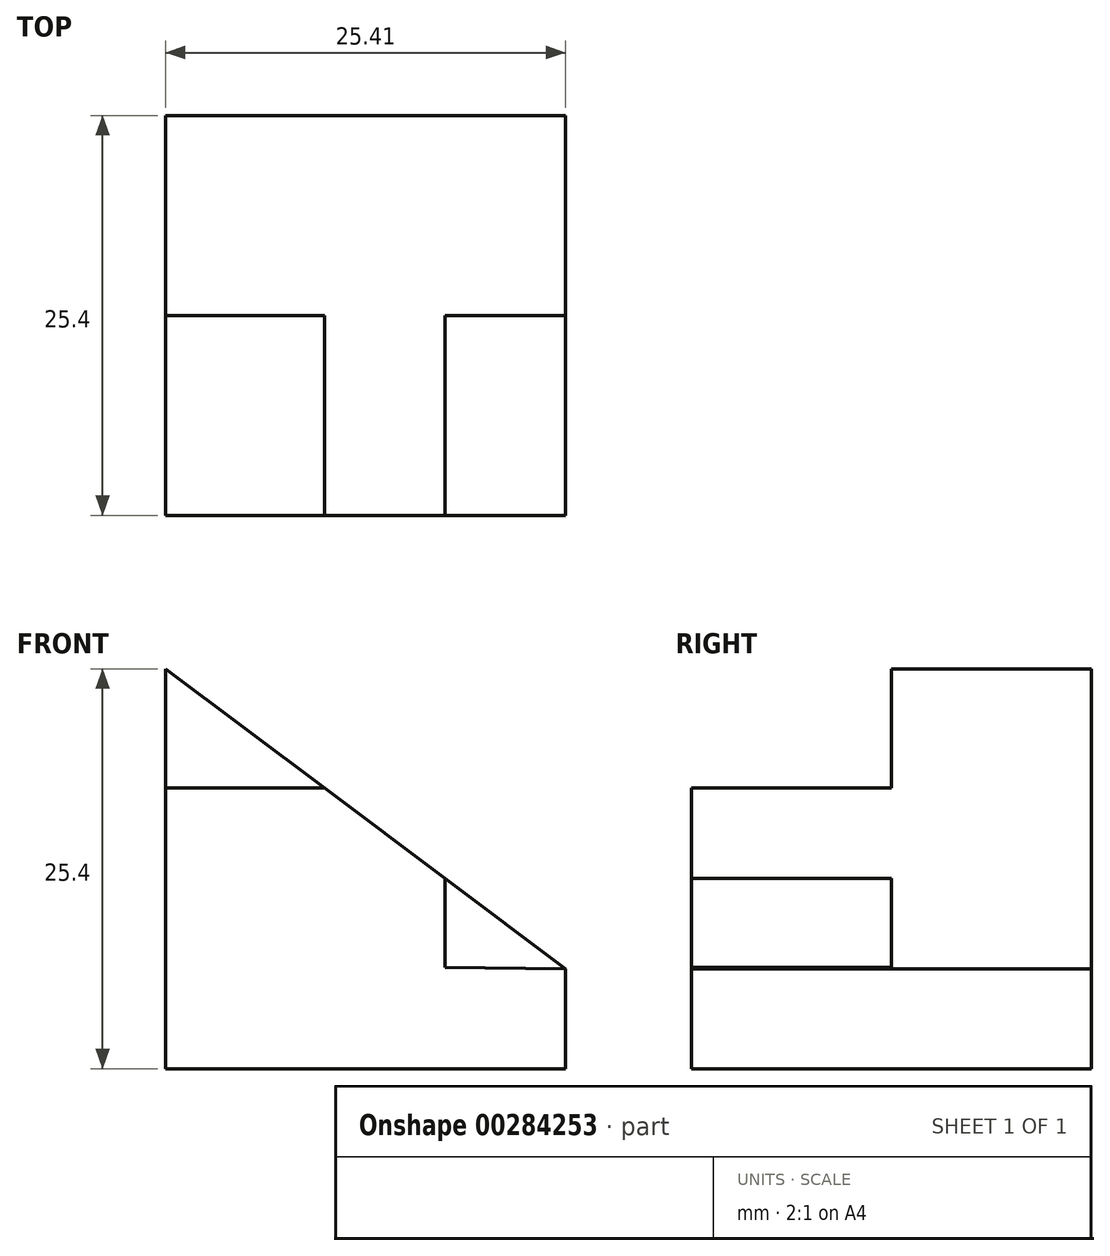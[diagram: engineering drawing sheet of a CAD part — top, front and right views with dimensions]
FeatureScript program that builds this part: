
annotation { "Feature Type Name" : "Feature", "Feature Type Description" : "" }
export const myFeature = defineFeature(function(context is Context, id is Id, definition is map)
    precondition{}
    {
        {
            var Q0;
            Q0=qCreatedBy(makeId("Front.planeOp"),FACE);
            var sketch = newSketch(context, id + "F0", { "sketchPlane" : qUnion([Q0])});
            skLineSegment(sketch, "E0", {"start": v(0, 0) * mm, "end": v(25.4, 0) * mm});
            skLineSegment(sketch, "E1", {"start": v(25.4, 0) * mm, "end": v(25.4, 6.35) * mm});
            skLineSegment(sketch, "E2", {"start": v(25.4, 6.35) * mm, "end": v(0, 6.35) * mm});
            skLineSegment(sketch, "E3", {"start": v(0, 6.35) * mm, "end": v(0, 0) * mm});
            skSolve(sketch);
        }
        {
            var Q0;
            Q0 = qSketchRegion(id + "F0", true);
            extrude(context, id + "F1", {"entities" : qUnion([Q0]), "depth" : 25.4 * mm});
        }
        {
            var Q0;
            Q0=qCreatedBy(makeId("Front.planeOp"),FACE);
            var sketch = newSketch(context, id + "F2", { "sketchPlane" : qUnion([Q0])});
            skLineSegment(sketch, "E4", {"start": v(0, 6.35) * mm, "end": v(0, 25.4) * mm});
            skLineSegment(sketch, "E5", {"start": v(0, 25.4) * mm, "end": v(25.41, 6.35) * mm});
            skLineSegment(sketch, "E6", {"start": v(25.41, 6.35) * mm, "end": v(0, 6.35) * mm});
            skSolve(sketch);
        }
        {
            var Q0;
            Q0=makeQuery(id+"F2.imprint","IMPRINT",FACE,{"disambiguationData":[TD([[makeQuery(id+"F2.imprint","IMPRINT",EDGE,{"derivedFrom":sQuery(id+"F2.wireOp",EDGE,"E4")}),-1.0]])]});
            extrude(context, id + "F3", {"entities" : qUnion([Q0]), "operationType" : NewBodyOperationType.ADD, "depth" : 25.4 * mm});
        }
        {
            var Q0;
            Q0=makeQuery(id+"F3.boolean.opBoolean","MERGE",FACE,{"derivedFrom":[makeQuery(id+"F1.opExtrude","CAP_FACE",FACE,{"disambiguationData":[OSD([sQuery(id+"F0.wireOp",EDGE,"E0"),sQuery(id+"F0.wireOp",EDGE,"E1"),sQuery(id+"F0.wireOp",EDGE,"E2"),sQuery(id+"F0.wireOp",EDGE,"E3")])],"isStart":false}),makeQuery(id+"F3.opExtrude","CAP_FACE",FACE,{"disambiguationData":[OSD([sQuery(id+"F2.wireOp",EDGE,"E4"),sQuery(id+"F2.wireOp",EDGE,"E5"),sQuery(id+"F2.wireOp",EDGE,"E6")])],"isStart":false})]});
            var sketch = newSketch(context, id + "F4", { "sketchPlane" : qUnion([Q0])});
            skLineSegment(sketch, "E7", {"start": v(0, 17.82) * mm, "end": v(10.1, 17.82) * mm});
            skLineSegment(sketch, "E8", {"start": v(0, 25.4) * mm, "end": v(10.1, 17.82) * mm});
            skLineSegment(sketch, "E9", {"start": v(0, 25.4) * mm, "end": v(0, 17.82) * mm});
            skSolve(sketch);
        }
        {
            var Q0;
            Q0=makeQuery(id+"F4.imprint","IMPRINT",FACE,{"disambiguationData":[TD([[makeQuery(id+"F4.imprint","IMPRINT",EDGE,{"derivedFrom":sQuery(id+"F4.wireOp",EDGE,"E7")}),1.0]])]});
            extrude(context, id + "F5", {"entities" : qUnion([Q0]), "operationType" : NewBodyOperationType.REMOVE, "oppositeDirection" : true, "depth" : 12.7 * mm});
        }
        {
            var Q0;
            Q0=makeQuery(id+"F3.boolean.opBoolean","MERGE",FACE,{"derivedFrom":[makeQuery(id+"F1.opExtrude","CAP_FACE",FACE,{"disambiguationData":[OSD([sQuery(id+"F0.wireOp",EDGE,"E0"),sQuery(id+"F0.wireOp",EDGE,"E1"),sQuery(id+"F0.wireOp",EDGE,"E2"),sQuery(id+"F0.wireOp",EDGE,"E3")])],"isStart":false}),makeQuery(id+"F3.opExtrude","CAP_FACE",FACE,{"disambiguationData":[OSD([sQuery(id+"F2.wireOp",EDGE,"E4"),sQuery(id+"F2.wireOp",EDGE,"E5"),sQuery(id+"F2.wireOp",EDGE,"E6")])],"isStart":false})]});
            var sketch = newSketch(context, id + "F6", { "sketchPlane" : qUnion([Q0])});
            skLineSegment(sketch, "E10", {"start": v(17.76, 12.09) * mm, "end": v(17.76, 6.45) * mm});
            skLineSegment(sketch, "E11", {"start": v(17.76, 6.45) * mm, "end": v(25.41, 6.35) * mm});
            skLineSegment(sketch, "E12", {"start": v(17.75, 12.1) * mm, "end": v(25.41, 6.35) * mm});
            skSolve(sketch);
        }
        {
            var Q0;
            {var subQ0=sQuery(id+"F6.wireOp",EDGE,"E10");Q0=makeQuery(id+"F6.imprint","IMPRINT",FACE,{"disambiguationData":[TD([[makeQuery(id+"F6.imprint","IMPRINT",EDGE,{"derivedFrom":subQ0}),1.0]])]});}
            extrude(context, id + "F7", {"entities" : qUnion([Q0]), "operationType" : NewBodyOperationType.REMOVE, "oppositeDirection" : true, "depth" : 12.7 * mm});
        }
    });
